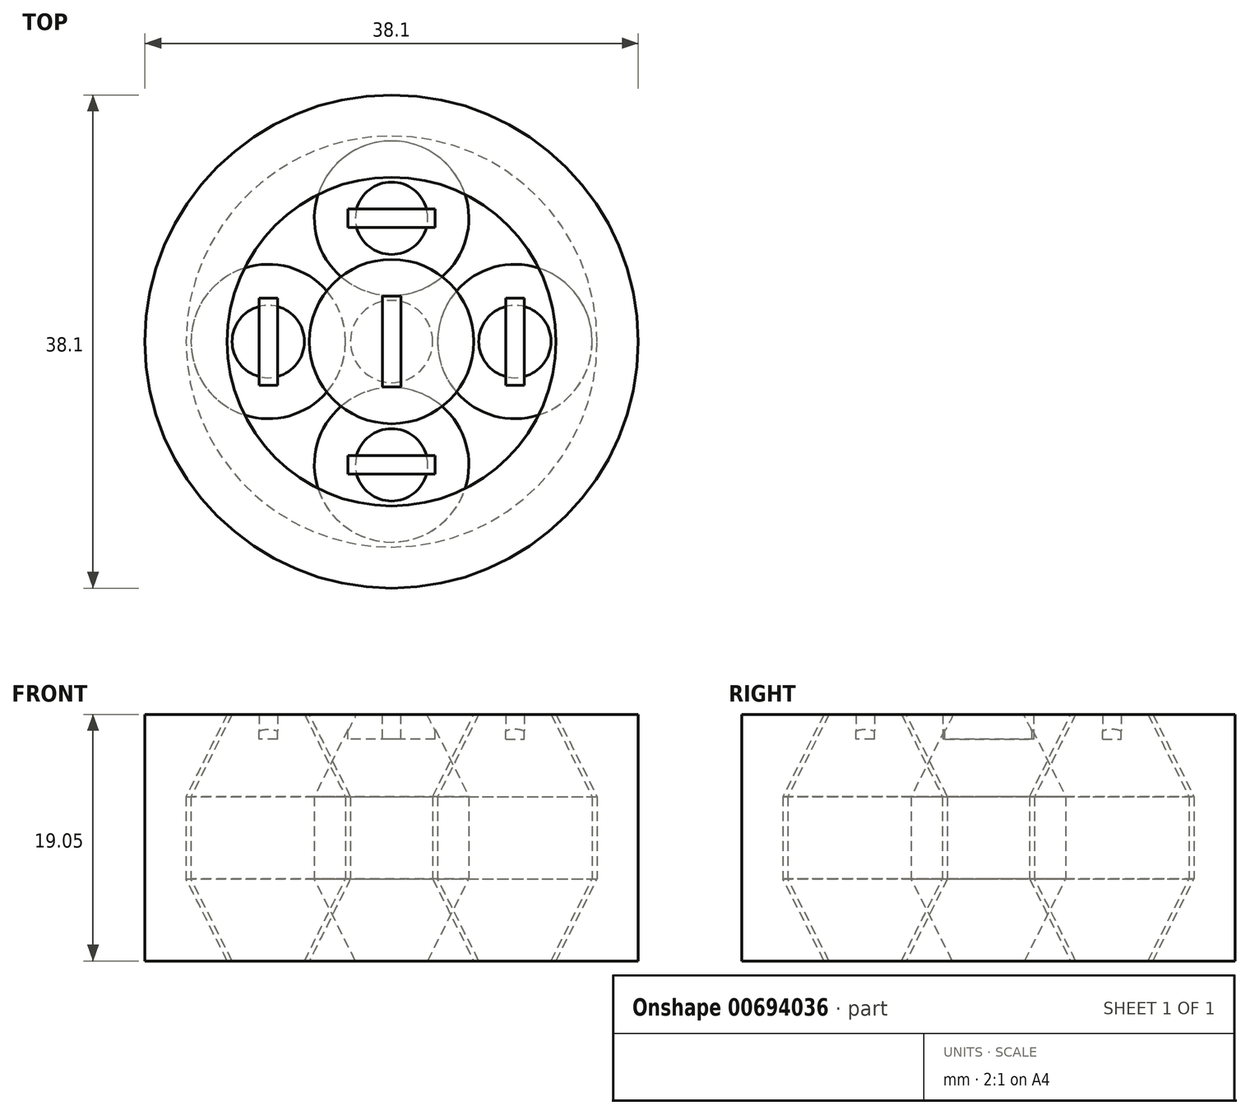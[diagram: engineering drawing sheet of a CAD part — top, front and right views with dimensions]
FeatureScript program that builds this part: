
annotation { "Feature Type Name" : "Feature", "Feature Type Description" : "" }
export const myFeature = defineFeature(function(context is Context, id is Id, definition is map)
    precondition{}
    {
        {
            var Q0;
            Q0=qCreatedBy(makeId("Front.planeOp"),FACE);
            var sketch = newSketch(context, id + "F0", { "sketchPlane" : qUnion([Q0])});
            skLineSegment(sketch, "E0.bottom", {"start": v(0, 0) * mm, "end": v(3.18, 0) * mm});
            skLineSegment(sketch, "E0.top", {"start": v(0, 19.05) * mm, "end": v(3.17, 19.05) * mm});
            skLineSegment(sketch, "E0.left", {"start": v(0, 0) * mm, "end": v(0, 19.05) * mm});
            skLineSegment(sketch, "E0.right", {"start": v(3.17, 6.35) * mm, "end": v(3.17, 12.7) * mm});
            skLineSegment(sketch, "E1.bottom", {"start": v(3.18, 0) * mm, "end": v(6.35, 0) * mm});
            skLineSegment(sketch, "E1.top", {"start": v(3.18, 0) * mm, "end": v(6.35, 0) * mm});
            skLineSegment(sketch, "E1.left", {"start": v(3.18, 0) * mm, "end": v(3.18, 0) * mm});
            skLineSegment(sketch, "E1.right", {"start": v(6.35, 0) * mm, "end": v(6.35, 0) * mm});
            skLineSegment(sketch, "E2", {"start": v(6.35, 0) * mm, "end": v(3.17, 6.35) * mm});
            skLineSegment(sketch, "E3", {"start": v(3.17, 19.05) * mm, "end": v(6.35, 19.05) * mm});
            skLineSegment(sketch, "E4", {"start": v(6.35, 19.05) * mm, "end": v(3.17, 12.7) * mm});
            skLineSegment(sketch, "E5", {"start": v(6.73, 19.05) * mm, "end": v(3.56, 12.7) * mm});
            skLineSegment(sketch, "E6", {"start": v(3.56, 12.7) * mm, "end": v(3.56, 6.35) * mm});
            skLineSegment(sketch, "E7", {"start": v(3.56, 6.35) * mm, "end": v(6.73, 0) * mm});
            skLineSegment(sketch, "E8", {"start": v(6.73, 0) * mm, "end": v(9.53, 0) * mm});
            skLineSegment(sketch, "E9", {"start": v(9.53, 0) * mm, "end": v(9.53, 19.05) * mm});
            skLineSegment(sketch, "E10", {"start": v(6.73, 19.05) * mm, "end": v(9.53, 19.05) * mm});
            skPoint(sketch, "E11.orphan", {"position": v(12.32, 0) * mm});
            skLineSegment(sketch, "E12.MirrorCS", {"start": v(15.88, 19.05) * mm, "end": v(12.7, 19.05) * mm});
            skLineSegment(sketch, "E13.MirrorCS", {"start": v(12.32, 19.05) * mm, "end": v(9.53, 19.05) * mm});
            skLineSegment(sketch, "E14.MirrorCS", {"start": v(12.32, 19.05) * mm, "end": v(15.5, 12.7) * mm});
            skLineSegment(sketch, "E15.MirrorCS", {"start": v(12.7, 19.05) * mm, "end": v(15.88, 12.7) * mm});
            skLineSegment(sketch, "E16.MirrorCS", {"start": v(15.5, 12.7) * mm, "end": v(15.5, 6.35) * mm});
            skLineSegment(sketch, "E17.MirrorCS", {"start": v(15.88, 6.35) * mm, "end": v(15.88, 12.7) * mm});
            skLineSegment(sketch, "E18.MirrorCS", {"start": v(15.5, 6.35) * mm, "end": v(12.32, 0) * mm});
            skLineSegment(sketch, "E19.MirrorCS", {"start": v(12.7, 0) * mm, "end": v(15.88, 6.35) * mm});
            skLineSegment(sketch, "E20.MirrorCS", {"start": v(12.32, 0) * mm, "end": v(9.52, 0) * mm});
            skLineSegment(sketch, "E21.MirrorCS", {"start": v(15.88, 0) * mm, "end": v(12.7, 0) * mm});
            skLineSegment(sketch, "E22.MirrorCS", {"start": v(19.05, 0) * mm, "end": v(15.88, 0) * mm});
            skLineSegment(sketch, "E23.MirrorCS", {"start": v(19.05, 0) * mm, "end": v(19.05, 19.05) * mm});
            skLineSegment(sketch, "E24.MirrorCS", {"start": v(19.05, 19.05) * mm, "end": v(15.88, 19.05) * mm});
            skSolve(sketch);
        }
        {
            var Q0;
            Q0=makeQuery(id+"F0.imprint","IMPRINT",FACE,{"disambiguationData":[TD([[makeQuery(id+"F0.imprint","IMPRINT",EDGE,{"derivedFrom":sQuery(id+"F0.wireOp",EDGE,"E0.bottom")}),1.0]])]});
            var Q1;
            Q1=makeQuery(id+"F0.imprint","IMPRINT",FACE,{"disambiguationData":[TD([[makeQuery(id+"F0.imprint","IMPRINT",EDGE,{"derivedFrom":sQuery(id+"F0.wireOp",EDGE,"E12.MirrorCS")}),1.0]])]});
            var Q2;
            Q2=sQuery(id+"F0.wireOp",EDGE,"E0.left");
            revolve(context, id + "F1", {"entities" : qUnion([Q0, Q1]), "axis" : qUnion([Q2]), "revolveType" : RevolveType.FULL});
        }
        {
            var Q0;
            Q0=makeQuery(id+"F0.imprint","IMPRINT",FACE,{"disambiguationData":[TD([[makeQuery(id+"F0.imprint","IMPRINT",EDGE,{"derivedFrom":sQuery(id+"F0.wireOp",EDGE,"E9")}),-1.0]])]});
            var Q1;
            Q1=sQuery(id+"F0.wireOp",EDGE,"E9");
            revolve(context, id + "F2", {"entities" : qUnion([Q0]), "axis" : qUnion([Q1]), "revolveType" : RevolveType.FULL});
        }
        {
            var Q0;
            Q0=makeQuery(id+"F1.opRevolve","SWEPT_FACE",FACE,{"disambiguationData":[OSD([sQuery(id+"F0.wireOp",EDGE,"E0.top"),sQuery(id+"F0.wireOp",EDGE,"E3")])]});
            var sketch = newSketch(context, id + "F3", { "sketchPlane" : qUnion([Q0])});
            skLineSegment(sketch, "E25.bottom", {"start": v(0.71, 3.5) * mm, "end": v(-0.71, 3.5) * mm});
            skLineSegment(sketch, "E25.top", {"start": v(0.71, -3.5) * mm, "end": v(-0.71, -3.5) * mm});
            skLineSegment(sketch, "E25.left", {"start": v(0.71, 3.5) * mm, "end": v(0.71, -3.5) * mm});
            skLineSegment(sketch, "E25.right", {"start": v(-0.71, 3.5) * mm, "end": v(-0.71, -3.5) * mm});
            skPoint(sketch, "E25.middle", {"position": v(0, 0) * mm});
            skSolve(sketch);
        }
        {
            var Q0;
            Q0=makeQuery(id+"F3.imprint","IMPRINT",FACE,{"disambiguationData":[TD([[makeQuery(id+"F3.imprint","IMPRINT",EDGE,{"derivedFrom":sQuery(id+"F3.wireOp",EDGE,"E25.bottom")}),1.0]])]});
            extrude(context, id + "F4", {"entities" : qUnion([Q0]), "operationType" : NewBodyOperationType.REMOVE, "oppositeDirection" : true, "depth" : 1.9 * mm, "offsetDistance" : 25.4 * mm});
        }
        {
            var Q0;
            Q0=makeQuery(id+"F2.opRevolve","SWEPT_FACE",FACE,{"disambiguationData":[OSD([sQuery(id+"F0.wireOp",EDGE,"E13.MirrorCS")])]});
            var sketch = newSketch(context, id + "F5", { "sketchPlane" : qUnion([Q0])});
            skLineSegment(sketch, "E26.bottom", {"start": v(8.81, 3.37) * mm, "end": v(10.24, 3.37) * mm});
            skLineSegment(sketch, "E26.top", {"start": v(8.81, -3.37) * mm, "end": v(10.24, -3.37) * mm});
            skLineSegment(sketch, "E26.left", {"start": v(8.81, 3.37) * mm, "end": v(8.81, -3.37) * mm});
            skLineSegment(sketch, "E26.right", {"start": v(10.24, 3.37) * mm, "end": v(10.24, -3.37) * mm});
            skPoint(sketch, "E26.middle", {"position": v(9.53, 0) * mm});
            skSolve(sketch);
        }
        {
            var Q0;
            Q0 = qSketchRegion(id + "F5", true);
            extrude(context, id + "F6", {"entities" : qUnion([Q0]), "operationType" : NewBodyOperationType.REMOVE, "oppositeDirection" : true, "depth" : 1.9 * mm, "offsetDistance" : 25.4 * mm});
        }
        {
            var Q0;
            Q0=makeQuery(id+"F2.opRevolve","SWEPT_BODY",BODY,{"disambiguationData":[OSD([sQuery(id+"F0.wireOp",EDGE,"E9"),sQuery(id+"F0.wireOp",EDGE,"E13.MirrorCS"),sQuery(id+"F0.wireOp",EDGE,"E14.MirrorCS"),sQuery(id+"F0.wireOp",EDGE,"E16.MirrorCS"),sQuery(id+"F0.wireOp",EDGE,"E18.MirrorCS"),sQuery(id+"F0.wireOp",EDGE,"E20.MirrorCS")])]});
            var Q1;
            Q1=sQuery(id+"F0.wireOp",EDGE,"E0.left");
            circularPattern(context, id + "F7", {"entities" : qUnion([Q0]), "axis" : qUnion([Q1]), "angle" : 360 * degree, "instanceCount" : 4, "equalSpace" : true});
        }
    });
